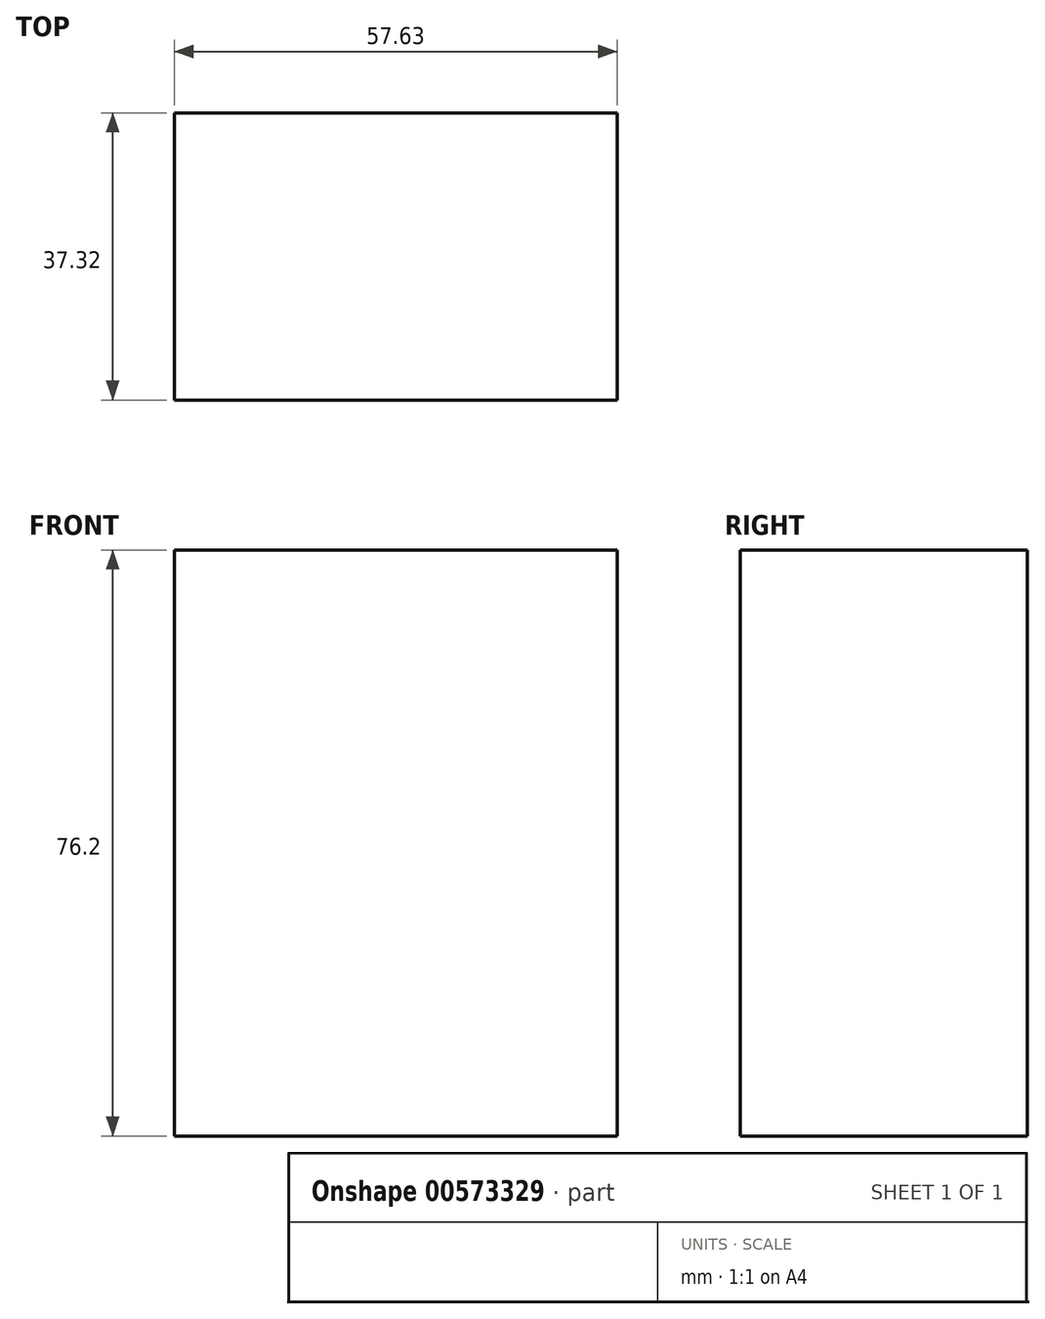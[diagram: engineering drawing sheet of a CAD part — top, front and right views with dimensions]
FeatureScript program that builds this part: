
annotation { "Feature Type Name" : "Feature", "Feature Type Description" : "" }
export const myFeature = defineFeature(function(context is Context, id is Id, definition is map)
    precondition{}
    {
        {
            var Q0;
            Q0=qCreatedBy(makeId("Top.planeOp"),FACE);
            var sketch = newSketch(context, id + "F0", { "sketchPlane" : qUnion([Q0])});
            skLineSegment(sketch, "E0.bottom", {"start": v(-57.63, 44.38) * mm, "end": v(0, 44.38) * mm});
            skLineSegment(sketch, "E0.top", {"start": v(-57.63, 7.06) * mm, "end": v(0, 7.06) * mm});
            skLineSegment(sketch, "E0.left", {"start": v(-57.63, 44.38) * mm, "end": v(-57.63, 7.06) * mm});
            skLineSegment(sketch, "E0.right", {"start": v(0, 44.38) * mm, "end": v(0, 7.06) * mm});
            skSolve(sketch);
        }
        {
            var Q0;
            Q0 = qSketchRegion(id + "F0", true);
            extrude(context, id + "F1", {"entities" : qUnion([Q0]), "depth" : 76.2 * mm, "offsetDistance" : 25.4 * mm});
        }
    });
